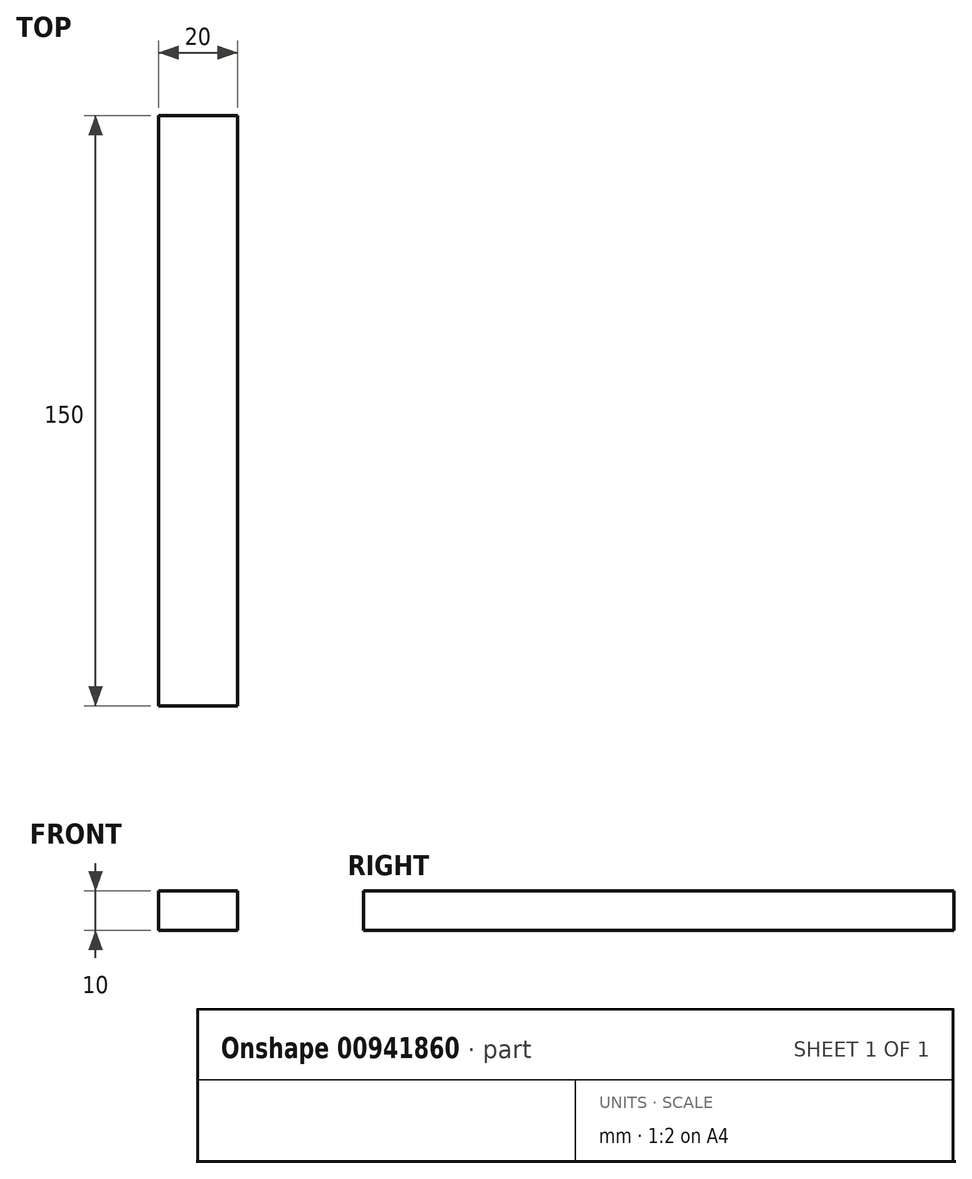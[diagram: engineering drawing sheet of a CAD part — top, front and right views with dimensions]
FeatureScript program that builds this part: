
annotation { "Feature Type Name" : "Feature", "Feature Type Description" : "" }
export const myFeature = defineFeature(function(context is Context, id is Id, definition is map)
    precondition{}
    {
        {
            var Q0;
            Q0=qCreatedBy(makeId("Top.planeOp"),FACE);
            var sketch = newSketch(context, id + "F0", { "sketchPlane" : qUnion([Q0])});
            skLineSegment(sketch, "E0", {"start": v(0, 0) * mm, "end": v(0, 150) * mm});
            skLineSegment(sketch, "E1", {"start": v(0, 150) * mm, "end": v(20, 150) * mm});
            skLineSegment(sketch, "E2", {"start": v(20, 150) * mm, "end": v(20, 15) * mm});
            skLineSegment(sketch, "E3", {"start": v(0, 0) * mm, "end": v(20, 0) * mm});
            skLineSegment(sketch, "E4", {"start": v(20, 0) * mm, "end": v(20, 15) * mm});
            skLineSegment(sketch, "E5", {"start": v(55.28, 0) * mm, "end": v(55.28, 156.5) * mm, "construction": true});
            skLineSegment(sketch, "E6", {"start": v(20, 15) * mm, "end": v(55.28, 15) * mm});
            skLineSegment(sketch, "E7", {"start": v(20, 32.69) * mm, "end": v(55.28, 32.69) * mm});
            skSolve(sketch);
        }
        {
            var Q0;
            Q0 = qSketchRegion(id + "F0", true);
            extrude(context, id + "F1", {"entities" : qUnion([Q0]), "depth" : 10 * mm, "offsetDistance" : 25 * mm});
        }
    });
